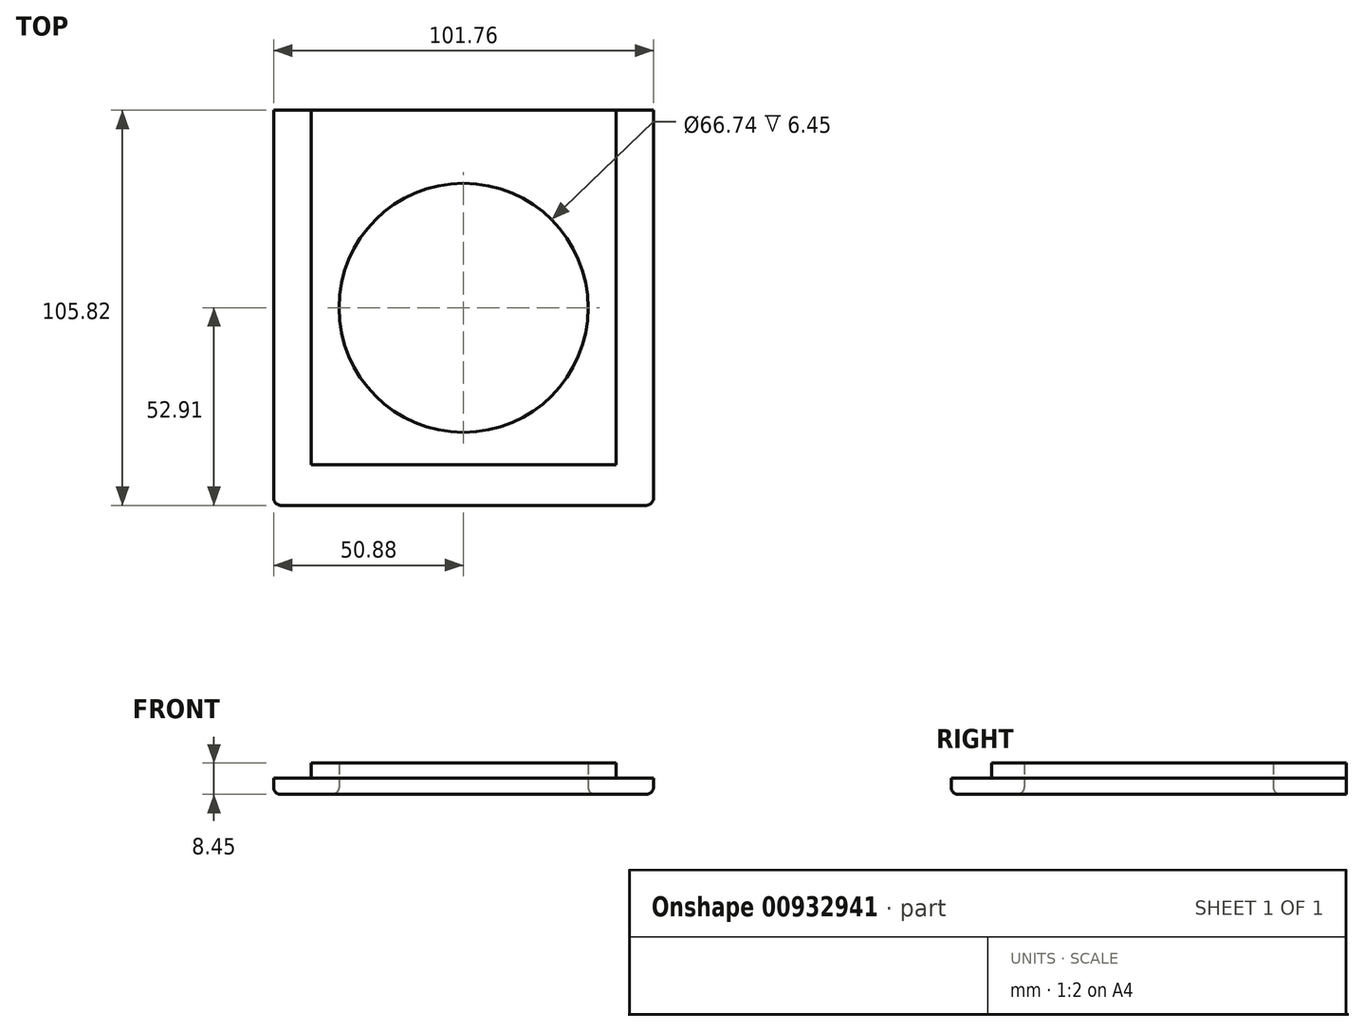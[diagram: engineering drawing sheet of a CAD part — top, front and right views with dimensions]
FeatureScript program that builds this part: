
annotation { "Feature Type Name" : "Feature", "Feature Type Description" : "" }
export const myFeature = defineFeature(function(context is Context, id is Id, definition is map)
    precondition{}
    {
        {
            var Q0;
            Q0=qCreatedBy(makeId("Top.planeOp"),FACE);
            var sketch = newSketch(context, id + "F0", { "sketchPlane" : qUnion([Q0])});
            skLineSegment(sketch, "E0.bottom", {"start": v(50.89, -52.9) * mm, "end": v(-50.88, -52.91) * mm});
            skLineSegment(sketch, "E0.top", {"start": v(50.88, 52.9) * mm, "end": v(-50.89, 52.9) * mm});
            skLineSegment(sketch, "E0.left", {"start": v(50.89, -52.9) * mm, "end": v(50.88, 52.91) * mm});
            skLineSegment(sketch, "E0.right", {"start": v(-50.89, -52.91) * mm, "end": v(-50.89, 52.9) * mm});
            skPoint(sketch, "E0.middle", {"position": v(0, 0) * mm});
            skCircle(sketch, "E1", {"center": v(0, 0) * mm, "radius": 33.37 * mm});
            skSolve(sketch);
        }
        {
            var Q0;
            Q0=makeQuery(id+"F0.imprint","IMPRINT",FACE,{"disambiguationData":[TD([[makeQuery(id+"F0.imprint","IMPRINT",EDGE,{"derivedFrom":sQuery(id+"F0.wireOp",EDGE,"E0.bottom")}),-1.0]])]});
            extrude(context, id + "F1", {"entities" : qUnion([Q0]), "depth" : 4.38 * mm, "offsetDistance" : 25 * mm});
        }
        {
            var Q0;
            Q0=makeQuery(id+"F1.opExtrude","CAP_FACE",FACE,{"disambiguationData":[OSD([sQuery(id+"F0.wireOp",EDGE,"E0.bottom"),sQuery(id+"F0.wireOp",EDGE,"E0.top"),sQuery(id+"F0.wireOp",EDGE,"E0.left"),sQuery(id+"F0.wireOp",EDGE,"E0.right"),sQuery(id+"F0.wireOp",EDGE,"E1")])],"isStart":false});
            var sketch = newSketch(context, id + "F2", { "sketchPlane" : qUnion([Q0])});
            skLineSegment(sketch, "E2.bottom", {"start": v(-40.82, 52.9) * mm, "end": v(40.81, 52.9) * mm});
            skLineSegment(sketch, "E2.top", {"start": v(-40.82, -42.08) * mm, "end": v(40.81, -42.08) * mm});
            skLineSegment(sketch, "E2.left", {"start": v(-40.82, 52.9) * mm, "end": v(-40.82, -42.08) * mm});
            skLineSegment(sketch, "E2.right", {"start": v(40.81, 52.9) * mm, "end": v(40.81, -42.08) * mm});
            skSolve(sketch);
        }
        {
            var Q0;
            Q0=makeQuery(id+"F2.imprint","IMPRINT",FACE,{"disambiguationData":[TD([[makeQuery(id+"F2.imprint","IMPRINT",EDGE,{"derivedFrom":sQuery(id+"F2.wireOp",EDGE,"E2.bottom")}),1.0]])]});
            extrude(context, id + "F3", {"entities" : qUnion([Q0]), "operationType" : NewBodyOperationType.ADD, "depth" : 4.07 * mm, "offsetDistance" : 25 * mm});
        }
        {
            var Q0;
            Q0=makeQuery(id+"F1.opExtrude","CAP_EDGE",EDGE,{"disambiguationData":[OSD([sQuery(id+"F0.wireOp",EDGE,"E1")])],"isStart":true});
            var Q1;
            Q1=makeQuery(id+"F1.opExtrude","CAP_EDGE",EDGE,{"disambiguationData":[OSD([sQuery(id+"F0.wireOp",EDGE,"E0.right")])],"isStart":true});
            var Q2;
            Q2=makeQuery(id+"F1.opExtrude","CAP_EDGE",EDGE,{"disambiguationData":[OSD([sQuery(id+"F0.wireOp",EDGE,"E0.bottom")])],"isStart":true});
            var Q3;
            Q3=makeQuery(id+"F1.opExtrude","CAP_EDGE",EDGE,{"disambiguationData":[OSD([sQuery(id+"F0.wireOp",EDGE,"E0.left")])],"isStart":true});
            fillet(context, id + "F4", {"entities" : qUnion([Q0, Q1, Q2, Q3]), "radius" : 2 * mm, "tangentPropagation" : true, "allowEdgeOverflow" : false});
        }
        {
            var Q0;
            Q0=makeQuery(id+"F1.opExtrude","SWEPT_EDGE",EDGE,{"disambiguationData":[OSD([sQuery(id+"F0.wireOp",EDGE,"E0.bottom"),sQuery(id+"F0.wireOp",EDGE,"E0.left")])]});
            var Q1;
            Q1=makeQuery(id+"F1.opExtrude","SWEPT_EDGE",EDGE,{"disambiguationData":[OSD([sQuery(id+"F0.wireOp",EDGE,"E0.bottom"),sQuery(id+"F0.wireOp",EDGE,"E0.right")])]});
            fillet(context, id + "F5", {"entities" : qUnion([Q0, Q1]), "radius" : 2 * mm, "tangentPropagation" : true, "allowEdgeOverflow" : false});
        }
    });
